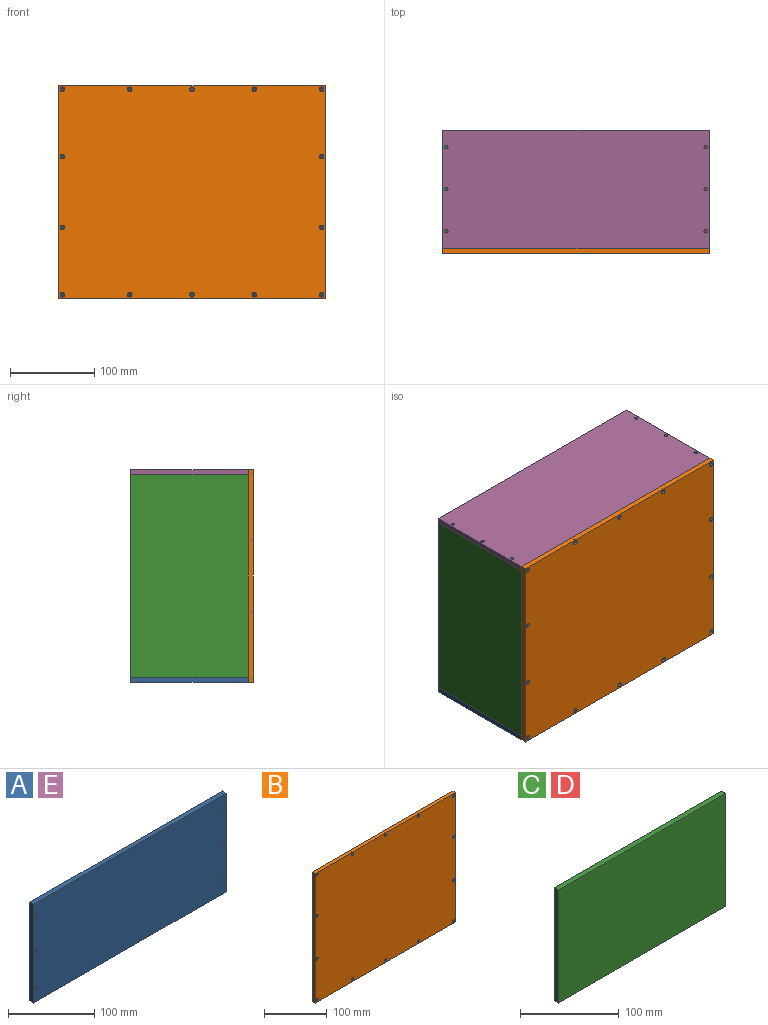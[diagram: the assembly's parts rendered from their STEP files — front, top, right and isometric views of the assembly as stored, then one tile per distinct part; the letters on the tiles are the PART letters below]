
ASSEMBLY  parts=5 mates=12
PART A: 12 faces, bbox 316x6x140 mm
  f0: plane 140x6mm, normal (1,0,0), area 840mm2, adj f1,f3,f4,f5
  f1: plane 316x6mm, normal (0,0,1), area 1896mm2, adj f0,f2,f4,f5
  f2: plane 140x6mm, normal (-1,0,0), area 840mm2, adj f1,f3,f4,f5
  f3: plane 316x6mm, normal (0,0,-1), area 1896mm2, adj f0,f2,f4,f5
  f4: plane 316x140mm, normal (0,-1,0), area 44164.6mm2, adj f0,f1,f2,f3,f6,f7,f8,f9
  f5: plane 316x140mm, normal (0,1,0), area 44164.6mm2, adj f0,f1,f2,f3,f6,f7,f8,f9
  f6: cylinder r=2mm len=6mm, axis (0,-1,0), area 75.4mm2, adj f4,f5
  f7: cylinder r=2mm len=6mm, axis (0,-1,0), area 75.4mm2, adj f4,f5
  f8: cylinder r=2mm len=6mm, axis (0,-1,0), area 75.4mm2, adj f4,f5
  f9: cylinder r=2mm len=6mm, axis (0,-1,0), area 75.4mm2, adj f4,f5
  f10: cylinder r=2mm len=6mm, axis (0,-1,0), area 75.4mm2, adj f4,f5
  f11: cylinder r=2mm len=6mm, axis (0,-1,0), area 75.4mm2, adj f4,f5
PART B: 48 faces, bbox 316x6x252 mm
  f0: plane 252x6mm, normal (1,0,0), area 1512mm2, adj f1,f3,f4,f5
  f1: plane 316x6mm, normal (0,0,1), area 1896mm2, adj f0,f2,f4,f5
  f2: plane 252x6mm, normal (-1,0,0), area 1512mm2, adj f1,f3,f4,f5
  f3: plane 316x6mm, normal (0,0,-1), area 1896mm2, adj f0,f2,f4,f5
  f4: plane 316x252mm, normal (0,-1,0), area 79299.4mm2, adj f0,f1,f2,f3,f8,f11,f14,f17
  f5: plane 316x252mm, normal (0,1,0), area 79539.5mm2, adj f0,f1,f2,f3,f6,f9,f12,f15
  f6: cylinder r=1.45mm len=3.5mm, axis (0,-1,0), area 31.9mm2, adj f5,f7
  f7: plane 5.5x5.5mm, normal (0,-1,0), area 17.2mm2, adj f6,f8
  f8: cylinder r=2.75mm len=5.5mm, axis (0,-1,0), area 43.2mm2, adj f4,f7
  f9: cylinder r=1.45mm len=3.5mm, axis (0,-1,0), area 31.9mm2, adj f5,f10
  f10: plane 5.5x5.5mm, normal (0,-1,0), area 17.2mm2, adj f9,f11
  f11: cylinder r=2.75mm len=5.5mm, axis (0,-1,0), area 43.2mm2, adj f4,f10
  f12: cylinder r=1.45mm len=3.5mm, axis (0,-1,0), area 31.9mm2, adj f5,f13
  f13: plane 5.5x5.5mm, normal (0,-1,0), area 17.2mm2, adj f12,f14
  f14: cylinder r=2.75mm len=5.5mm, axis (0,-1,0), area 43.2mm2, adj f4,f13
  f15: cylinder r=1.45mm len=3.5mm, axis (0,-1,0), area 31.9mm2, adj f5,f16
  f16: plane 5.5x5.5mm, normal (0,-1,0), area 17.2mm2, adj f15,f17
  f17: cylinder r=2.75mm len=5.5mm, axis (0,-1,0), area 43.2mm2, adj f4,f16
  f18: cylinder r=1.45mm len=3.5mm, axis (0,-1,0), area 31.9mm2, adj f5,f19
  f19: plane 5.5x5.5mm, normal (0,-1,0), area 17.2mm2, adj f18,f20
  f20: cylinder r=2.75mm len=5.5mm, axis (0,-1,0), area 43.2mm2, adj f4,f19
  f21: cylinder r=1.45mm len=3.5mm, axis (0,-1,0), area 31.9mm2, adj f5,f22
  f22: plane 5.5x5.5mm, normal (0,-1,0), area 17.2mm2, adj f21,f23
  f23: cylinder r=2.75mm len=5.5mm, axis (0,-1,0), area 43.2mm2, adj f4,f22
  f24: cylinder r=1.45mm len=3.5mm, axis (0,-1,0), area 31.9mm2, adj f5,f25
  f25: plane 5.5x5.5mm, normal (0,-1,0), area 17.2mm2, adj f24,f26
  f26: cylinder r=2.75mm len=5.5mm, axis (0,-1,0), area 43.2mm2, adj f4,f25
  f27: cylinder r=1.45mm len=3.5mm, axis (0,-1,0), area 31.9mm2, adj f5,f28
  f28: plane 5.5x5.5mm, normal (0,-1,0), area 17.2mm2, adj f27,f29
  f29: cylinder r=2.75mm len=5.5mm, axis (0,-1,0), area 43.2mm2, adj f4,f28
  f30: cylinder r=1.45mm len=3.5mm, axis (0,-1,0), area 31.9mm2, adj f5,f31
  f31: plane 5.5x5.5mm, normal (0,-1,0), area 17.2mm2, adj f30,f32
  f32: cylinder r=2.75mm len=5.5mm, axis (0,-1,0), area 43.2mm2, adj f4,f31
  f33: cylinder r=1.45mm len=3.5mm, axis (0,-1,0), area 31.9mm2, adj f5,f34
  f34: plane 5.5x5.5mm, normal (0,-1,0), area 17.2mm2, adj f33,f35
  f35: cylinder r=2.75mm len=5.5mm, axis (0,-1,0), area 43.2mm2, adj f4,f34
  f36: cylinder r=1.45mm len=3.5mm, axis (0,-1,0), area 31.9mm2, adj f5,f37
  f37: plane 5.5x5.5mm, normal (0,-1,0), area 17.2mm2, adj f36,f38
  f38: cylinder r=2.75mm len=5.5mm, axis (0,-1,0), area 43.2mm2, adj f4,f37
  f39: cylinder r=1.45mm len=3.5mm, axis (0,-1,0), area 31.9mm2, adj f5,f40
  f40: plane 5.5x5.5mm, normal (0,-1,0), area 17.2mm2, adj f39,f41
  f41: cylinder r=2.75mm len=5.5mm, axis (0,-1,0), area 43.2mm2, adj f4,f40
  f42: cylinder r=1.45mm len=3.5mm, axis (0,-1,0), area 31.9mm2, adj f5,f43
  f43: plane 5.5x5.5mm, normal (0,-1,0), area 17.2mm2, adj f42,f44
  f44: cylinder r=2.75mm len=5.5mm, axis (0,-1,0), area 43.2mm2, adj f4,f43
  f45: cylinder r=1.45mm len=3.5mm, axis (0,-1,0), area 31.9mm2, adj f5,f46
  f46: plane 5.5x5.5mm, normal (0,-1,0), area 17.2mm2, adj f45,f47
  f47: cylinder r=2.75mm len=5.5mm, axis (0,-1,0), area 43.2mm2, adj f4,f46
PART C: 6 faces, bbox 240x6x140 mm
  f0: plane 140x6mm, normal (1,0,0), area 840mm2, adj f1,f3,f4,f5
  f1: plane 240x6mm, normal (0,0,1), area 1440mm2, adj f0,f2,f4,f5
  f2: plane 140x6mm, normal (-1,0,0), area 840mm2, adj f1,f3,f4,f5
  f3: plane 240x6mm, normal (0,0,-1), area 1440mm2, adj f0,f2,f4,f5
  f4: plane 240x140mm, normal (0,-1,0), area 33600mm2, adj f0,f1,f2,f3
  f5: plane 240x140mm, normal (0,1,0), area 33600mm2, adj f0,f1,f2,f3
PART D: same geometry as C
PART E: same geometry as A
PLACE A rot(axis=(1,0,0),90deg) t=(0,70,-120)mm
PLACE B at identity fixed
PLACE C rot(axis=(-0.58,-0.58,-0.58),120deg) t=(-152,70,0)mm
PLACE D rot(axis=(0.58,-0.58,0.58),120deg) t=(152,70,0)mm
PLACE E rot(axis=(1,0,0),90deg) t=(0,70,126)mm
MATE planar D.f4 <-> B.f0  axis (1,0,0) through (158,70,0)mm
MATE planar B.f33 <-> E.f1  axis (0,1,0) through (0,0,122)mm
MATE planar C.f3 <-> B.f5  axis (0,-1,0) through (-158,0,0)mm
MATE planar C.f4 <-> B.f2  axis (-1,0,0) through (-158,0,-120)mm
MATE planar E.f0 <-> A.f0  axis (1,0,0) through (158,70,123)mm
MATE planar E.f5 <-> B.f1  axis (0,0,1) through (0,70,126)mm
MATE planar D.f1 <-> B.f5  axis (0,-1,0) through (155,0,0)mm
MATE planar A.f4 <-> B.f3  axis (0,0,-1) through (0,0,-126)mm
MATE planar C.f2 <-> A.f5  axis (0,0,-1) through (-158,70,-120)mm
MATE planar A.f1 <-> B.f12  axis (0,-1,0) through (0,0,-123)mm
MATE parallel E.f0 <-> B.f0  axis (1,0,0) through (158,0,123)mm
MATE planar E.f0 <-> B.f0  axis (1,0,0) through (158,0,123)mm
